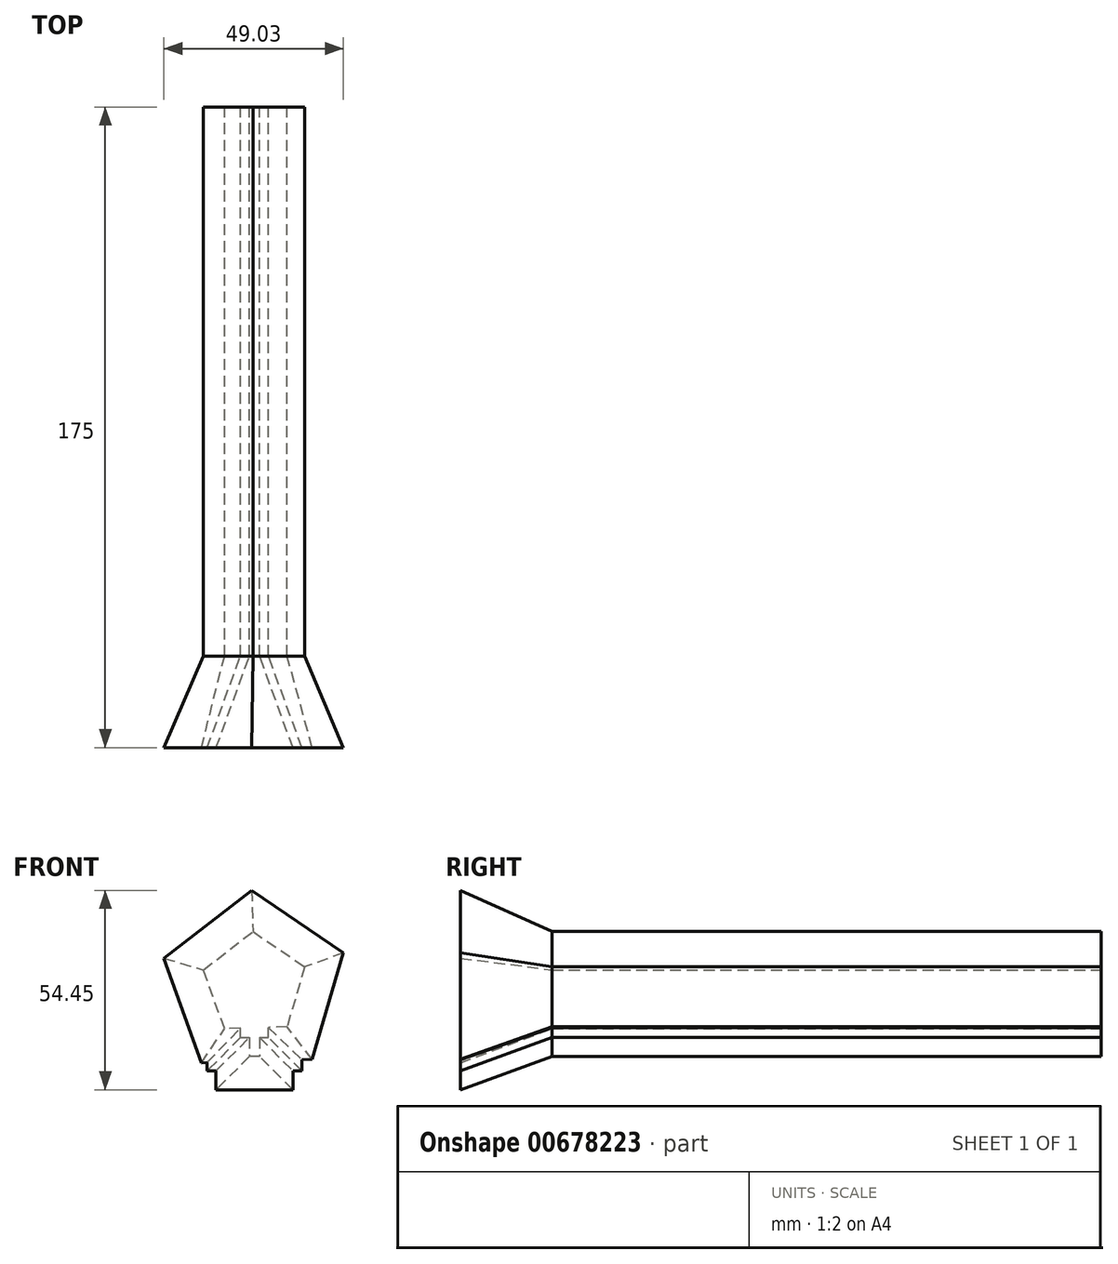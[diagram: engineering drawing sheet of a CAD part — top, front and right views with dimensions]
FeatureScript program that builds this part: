
annotation { "Feature Type Name" : "Feature", "Feature Type Description" : "" }
export const myFeature = defineFeature(function(context is Context, id is Id, definition is map)
    precondition{}
    {
        {
            var Q0;
            Q0=qCreatedBy(makeId("Front.planeOp"),FACE);
            var sketch = newSketch(context, id + "F0", { "sketchPlane" : qUnion([Q0])});
            skLineSegment(sketch, "E0.0", {"start": v(-13.96, 13.94) * mm, "end": v(-0.43, 24.4) * mm});
            skLineSegment(sketch, "E0.1", {"start": v(-0.43, 24.4) * mm, "end": v(13.69, 14.77) * mm});
            skLineSegment(sketch, "E0.2", {"start": v(13.69, 14.77) * mm, "end": v(8.9, -1.64) * mm});
            skLineSegment(sketch, "E0.3", {"start": v(8.9, -1.64) * mm, "end": v(-8.2, -2.15) * mm});
            skLineSegment(sketch, "E0.4", {"start": v(-8.2, -2.15) * mm, "end": v(-13.96, 13.94) * mm});
            skLineSegment(sketch, "E1.top", {"start": v(0, -9.71) * mm, "end": v(-1.4, -9.71) * mm});
            skLineSegment(sketch, "E1.right", {"start": v(-1.4, -4.57) * mm, "end": v(-1.4, -9.71) * mm});
            skLineSegment(sketch, "E2.MirrorCS", {"start": v(0, -9.71) * mm, "end": v(1.4, -9.71) * mm});
            skLineSegment(sketch, "E3.MirrorCS", {"start": v(1.4, -4.57) * mm, "end": v(1.4, -9.71) * mm});
            skLineSegment(sketch, "E4", {"start": v(-3.85, -4.57) * mm, "end": v(-1.4, -4.57) * mm});
            skLineSegment(sketch, "E5", {"start": v(1.4, -4.57) * mm, "end": v(3.85, -4.57) * mm});
            skLineSegment(sketch, "E6", {"start": v(-3.85, -4.57) * mm, "end": v(-3.85, -2.02) * mm});
            skLineSegment(sketch, "E7", {"start": v(3.85, -4.57) * mm, "end": v(3.85, -1.8) * mm});
            skSolve(sketch);
        }
        {
            var Q0;
            Q0=makeQuery(id+"F0.imprint","IMPRINT",FACE,{"disambiguationData":[TD([[makeQuery(id+"F0.imprint","IMPRINT",EDGE,{"derivedFrom":sQuery(id+"F0.wireOp",EDGE,"E0.0")}),-1.0]])]});
            var Q1;
            Q1=makeQuery(id+"F0.imprint","IMPRINT",FACE,{"disambiguationData":[TD([[makeQuery(id+"F0.imprint","IMPRINT",EDGE,{"derivedFrom":sQuery(id+"F0.wireOp",EDGE,"E1.top")}),-1.0]])]});
            extrude(context, id + "F1", {"entities" : qUnion([Q0, Q1]), "depth" : 150 * mm, "offsetDistance" : 25 * mm});
        }
        {
            var Q0;
            Q0=makeQuery(id+"F1.opExtrude","CAP_FACE",FACE,{"disambiguationData":[OSD([sQuery(id+"F0.wireOp",EDGE,"E0.0"),sQuery(id+"F0.wireOp",EDGE,"E0.1"),sQuery(id+"F0.wireOp",EDGE,"E0.2"),sQuery(id+"F0.wireOp",EDGE,"E0.3"),sQuery(id+"F0.wireOp",EDGE,"E0.4"),sQuery(id+"F0.wireOp",EDGE,"E1.top"),sQuery(id+"F0.wireOp",EDGE,"E1.right"),sQuery(id+"F0.wireOp",EDGE,"E2.MirrorCS"),sQuery(id+"F0.wireOp",EDGE,"E3.MirrorCS"),sQuery(id+"F0.wireOp",EDGE,"E4"),sQuery(id+"F0.wireOp",EDGE,"E5"),sQuery(id+"F0.wireOp",EDGE,"E6"),sQuery(id+"F0.wireOp",EDGE,"E7")])],"isStart":false});
            extrude(context, id + "F2", {"entities" : qUnion([Q0]), "operationType" : NewBodyOperationType.ADD, "depth" : 25 * mm, "offsetDistance" : 25 * mm, "hasDraft" : true, "draftAngle" : 20 * degree});
        }
    });
